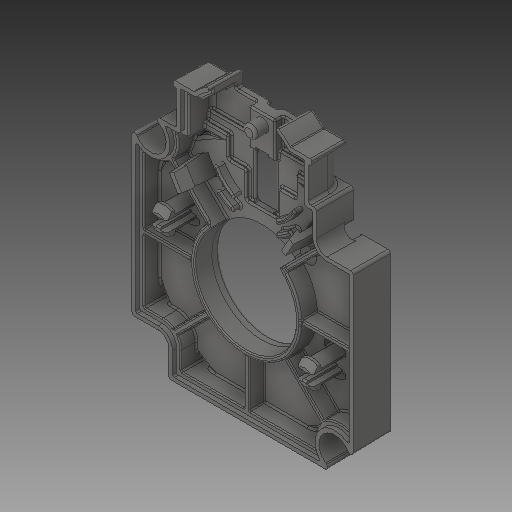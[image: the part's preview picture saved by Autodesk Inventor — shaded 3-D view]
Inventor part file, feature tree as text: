
AUTODESK INVENTOR PART (.ipt)
format: ipt  version: 2017 (Build 210142000, 142)  size: 2,017,280 bytes
history: native  units: in
note: dims shown in document units (in); Inventor stores cm internally (conversion verified against a paired STEP export)
features: fillet x1
ambient origin geometry x8: Origin, YZ Plane, XZ Plane, XY Plane, X Axis, Y Axis, Z Axis, Center Point
bodies: Solid1 (feature_tree)
feature tree (1):
  fillet  "Fillet32"  [1 undecoded]
note: 1 required parameter value undecoded (feature->parameter linkage not recoverable at this tier; creation-order binding heuristic only, values carry confidence <= 0.55)
